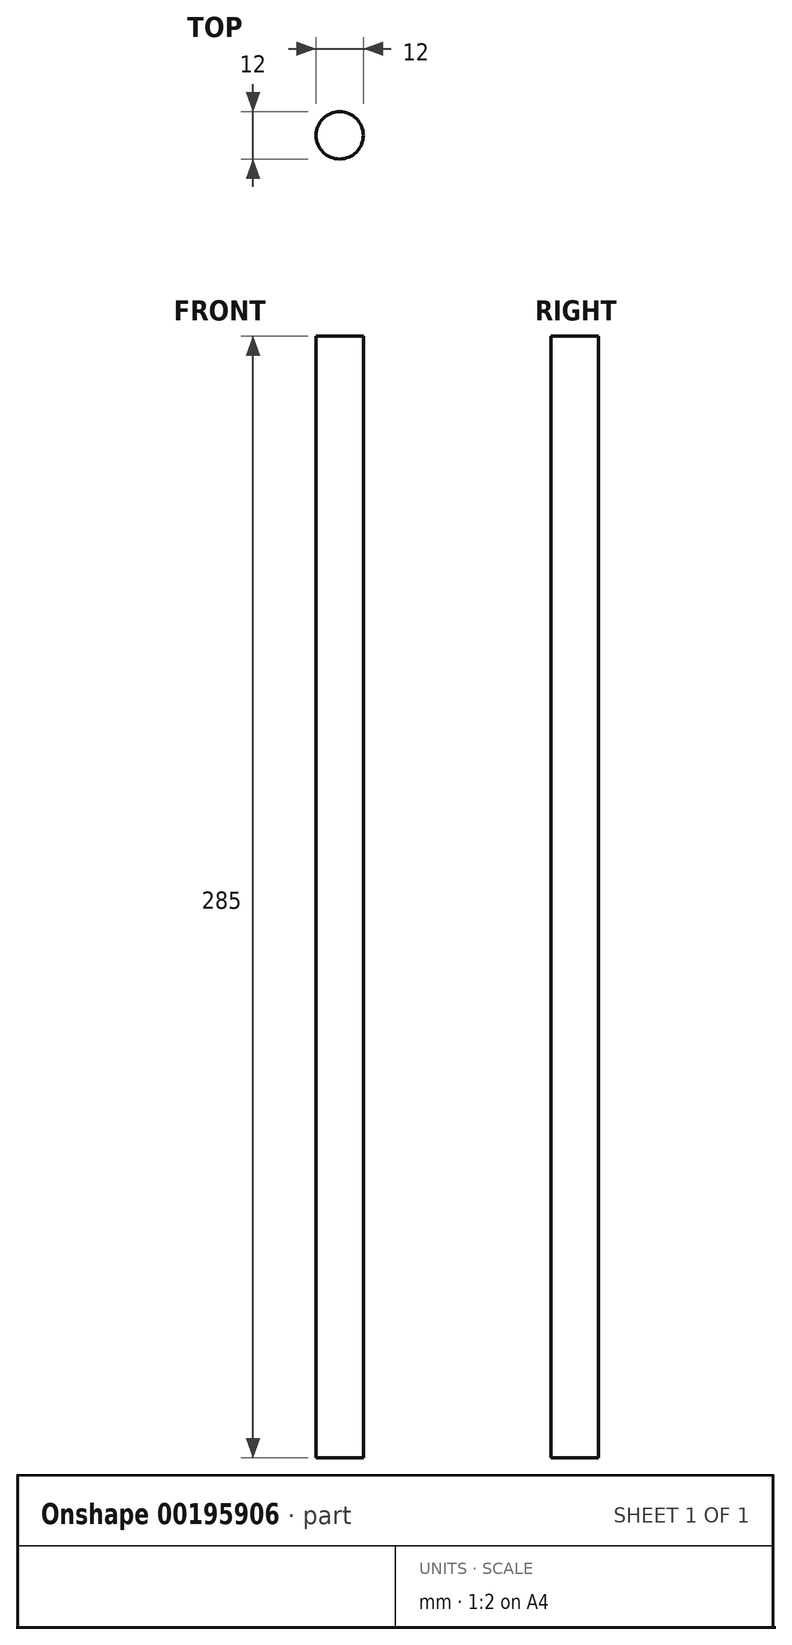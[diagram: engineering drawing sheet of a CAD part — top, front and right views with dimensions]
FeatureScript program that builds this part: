
annotation { "Feature Type Name" : "Feature", "Feature Type Description" : "" }
export const myFeature = defineFeature(function(context is Context, id is Id, definition is map)
    precondition{}
    {
        {
            var Q0;
            Q0=qCreatedBy(makeId("Top.planeOp"),FACE);
            var sketch = newSketch(context, id + "F0", { "sketchPlane" : qUnion([Q0])});
            skCircle(sketch, "E0", {"center": v(0, 0) * mm, "radius": 6 * mm});
            skSolve(sketch);
        }
        {
            var Q0;
            Q0=qSketchRegion(id+"F0",true);
            extrude(context, id + "F1", {"entities" : qUnion([Q0]), "depth" : 285 * mm});
        }
    });
